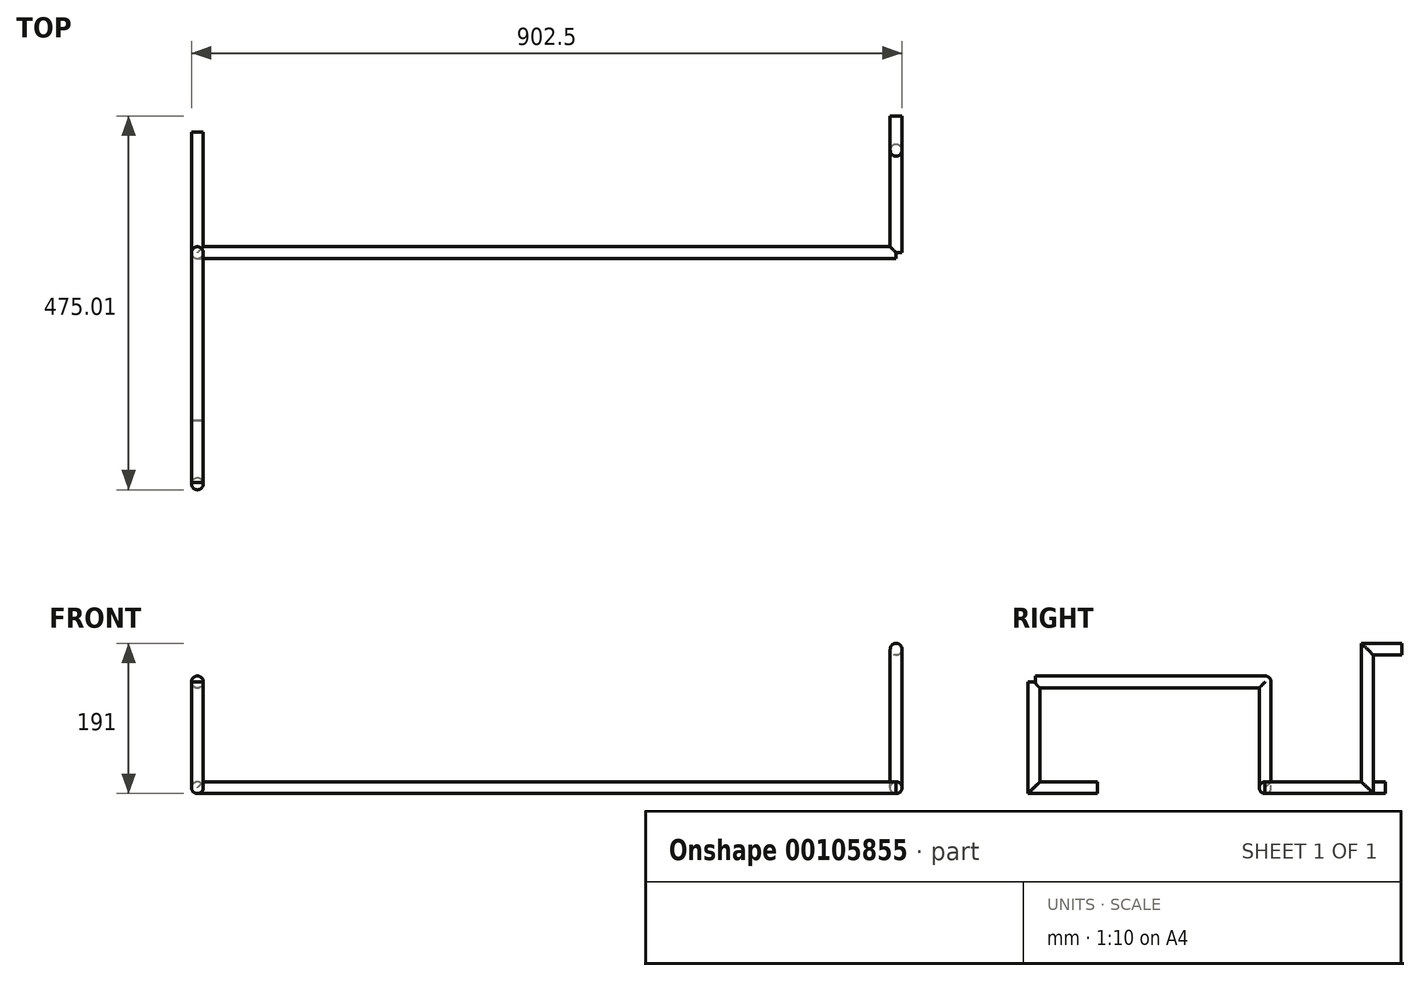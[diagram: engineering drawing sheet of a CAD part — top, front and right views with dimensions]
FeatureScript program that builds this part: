
annotation { "Feature Type Name" : "Feature", "Feature Type Description" : "" }
export const myFeature = defineFeature(function(context is Context, id is Id, definition is map)
    precondition{}
    {
        {
            var Q0;
            Q0=qCreatedBy(makeId("Front.planeOp"),FACE);
            var sketch = newSketch(context, id + "F0", { "sketchPlane" : qUnion([Q0])});
            skCircle(sketch, "E0", {"center": v(0, 0) * mm, "radius": 7.5 * mm});
            skSolve(sketch);
        }
        {
            var Q0;
            Q0=qCreatedBy(makeId("Right.planeOp"),FACE);
            var sketch = newSketch(context, id + "F1", { "sketchPlane" : qUnion([Q0])});
            skLineSegment(sketch, "E1", {"start": v(-80.78, 0) * mm, "end": v(0, 0) * mm});
            skLineSegment(sketch, "E2", {"start": v(-80.78, 0) * mm, "end": v(-80.78, 134.38) * mm});
            skSolve(sketch);
        }
        {
            var Q0;
            Q0=makeQuery(id+"F0.imprint","IMPRINT",FACE,{"disambiguationData":[TD([[makeQuery(id+"F0.imprint","IMPRINT",EDGE,{"derivedFrom":sQuery(id+"F0.wireOp",EDGE,"E0")}),1.0]])]});
            var Q1;
            Q1=sQuery(id+"F1.wireOp",EDGE,"E1");
            var Q2;
            Q2=sQuery(id+"F1.wireOp",EDGE,"E2");
            sweep(context, id + "F2", {"profiles" : qUnion([Q0]), "path" : qUnion([Q1, Q2])});
        }
        {
            var Q0;
            Q0=qCreatedBy(makeId("Top.planeOp"),FACE);
            var sketch = newSketch(context, id + "F3", { "sketchPlane" : qUnion([Q0])});
            skLineSegment(sketch, "E3", {"start": v(0, 276.33) * mm, "end": v(0, 123.33) * mm});
            skSolve(sketch);
        }
        {
            var Q0;
            Q0=qCreatedBy(makeId("Front.planeOp"),FACE);
            cPlane(context, id + "F4", {"entities" : qUnion([Q0]), "cplaneType" : CPlaneType.OFFSET, "offset" : 366 * mm, "oppositeDirection" : true, "width" : 150 * mm, "height" : 150 * mm});
        }
        {
            var Q0;
            Q0=qCreatedBy(id+"F4.planeOp",FACE);
            var sketch = newSketch(context, id + "F5", { "sketchPlane" : qUnion([Q0])});
            skCircle(sketch, "E4", {"center": v(0, 0) * mm, "radius": 7.5 * mm});
            skSolve(sketch);
        }
        {
            var Q0;
            Q0=makeQuery(id+"F5.imprint","IMPRINT",FACE,{"disambiguationData":[TD([[makeQuery(id+"F5.imprint","IMPRINT",EDGE,{"derivedFrom":sQuery(id+"F5.wireOp",EDGE,"E4")}),1.0]])]});
            var Q1;
            Q1=sQuery(id+"F3.wireOp",EDGE,"E3");
            sweep(context, id + "F6", {"profiles" : qUnion([Q0]), "path" : qUnion([Q1])});
        }
        {
            var Q0;
            Q0=qCreatedBy(makeId("Top.planeOp"),FACE);
            var sketch = newSketch(context, id + "F7", { "sketchPlane" : qUnion([Q0])});
            skCircle(sketch, "E5", {"center": v(0, 213) * mm, "radius": 7.5 * mm});
            skSolve(sketch);
        }
        {
            var Q0;
            Q0=makeQuery(id+"F7.imprint","IMPRINT",FACE,{"disambiguationData":[TD([[makeQuery(id+"F7.imprint","IMPRINT",EDGE,{"derivedFrom":sQuery(id+"F7.wireOp",EDGE,"E5")}),1.0]])]});
            var Q1;
            Q1=sQuery(id+"F1.wireOp",EDGE,"E2");
            sweep(context, id + "F8", {"operationType" : NewBodyOperationType.ADD, "profiles" : qUnion([Q0]), "path" : qUnion([Q1])});
        }
        {
            var Q0;
            Q0=qCreatedBy(makeId("Front.planeOp"),FACE);
            cPlane(context, id + "F9", {"entities" : qUnion([Q0]), "cplaneType" : CPlaneType.OFFSET, "offset" : 213 * mm, "oppositeDirection" : true, "width" : 150 * mm, "height" : 150 * mm});
        }
        {
            var Q0;
            Q0=qCreatedBy(id+"F9.planeOp",FACE);
            var sketch = newSketch(context, id + "F10", { "sketchPlane" : qUnion([Q0])});
            skCircle(sketch, "E6", {"center": v(0, 134.38) * mm, "radius": 7.5 * mm});
            skSolve(sketch);
        }
        {
            var Q0;
            Q0=qCreatedBy(makeId("Right.planeOp"),FACE);
            var sketch = newSketch(context, id + "F11", { "sketchPlane" : qUnion([Q0])});
            skLineSegment(sketch, "E7", {"start": v(211.22, 134.38) * mm, "end": v(-80.78, 134.38) * mm});
            skSolve(sketch);
        }
        {
            var Q0;
            Q0=makeQuery(id+"F10.imprint","IMPRINT",FACE,{"disambiguationData":[TD([[makeQuery(id+"F10.imprint","IMPRINT",EDGE,{"derivedFrom":sQuery(id+"F10.wireOp",EDGE,"E6")}),1.0]])]});
            var Q1;
            Q1=sQuery(id+"F11.wireOp",EDGE,"E7");
            sweep(context, id + "F12", {"operationType" : NewBodyOperationType.ADD, "profiles" : qUnion([Q0]), "path" : qUnion([Q1])});
        }
        {
            var Q0;
            Q0=makeQuery(id+"F8.opSweep","CAP_FACE",FACE,{"disambiguationData":[OSD([sQuery(id+"F1.wireOp",VERTEX,"E2.end"),sQuery(id+"F7.wireOp",EDGE,"E5")])],"isStart":false});
            var Q1;
            Q1=makeQuery(id+"F12.boolean.opBoolean","INTERSECT",EDGE,{"derivedFrom":[makeQuery(id+"F8.opSweep","CAP_FACE",FACE,{"disambiguationData":[OSD([sQuery(id+"F1.wireOp",VERTEX,"E2.end"),sQuery(id+"F7.wireOp",EDGE,"E5")])],"isStart":false}),makeQuery(id+"F12.opSweep","CAP_FACE",FACE,{"disambiguationData":[OSD([sQuery(id+"F10.wireOp",EDGE,"E6"),sQuery(id+"F11.wireOp",VERTEX,"E7.start")])],"isStart":true})]});
            revolve(context, id + "F13", {"operationType" : NewBodyOperationType.ADD, "entities" : qUnion([Q0]), "axis" : qUnion([Q1]), "revolveType" : RevolveType.FULL});
        }
        {
            var Q0;
            Q0=makeQuery(id+"F8.opSweep","CAP_FACE",FACE,{"disambiguationData":[OSD([sQuery(id+"F1.wireOp",VERTEX,"E2.start"),sQuery(id+"F7.wireOp",EDGE,"E5")])],"isStart":true});
            var Q1;
            Q1=makeQuery(id+"F8.boolean.opBoolean","INTERSECT",EDGE,{"derivedFrom":[makeQuery(id+"F6.opSweep","CAP_FACE",FACE,{"disambiguationData":[OSD([sQuery(id+"F3.wireOp",VERTEX,"E3.end"),sQuery(id+"F5.wireOp",EDGE,"E4")])],"isStart":false}),makeQuery(id+"F8.opSweep","CAP_FACE",FACE,{"disambiguationData":[OSD([sQuery(id+"F1.wireOp",VERTEX,"E2.start"),sQuery(id+"F7.wireOp",EDGE,"E5")])],"isStart":true})]});
            revolve(context, id + "F14", {"operationType" : NewBodyOperationType.ADD, "entities" : qUnion([Q0]), "axis" : qUnion([Q1]), "revolveType" : RevolveType.FULL});
        }
        {
            var Q0;
            Q0=qCreatedBy(makeId("Right.planeOp"),FACE);
            var sketch = newSketch(context, id + "F15", { "sketchPlane" : qUnion([Q0])});
            skCircle(sketch, "E8", {"center": v(213, 0) * mm, "radius": 7.5 * mm});
            skSolve(sketch);
        }
        {
            var Q0;
            Q0=qCreatedBy(id+"F9.planeOp",FACE);
            var sketch = newSketch(context, id + "F16", { "sketchPlane" : qUnion([Q0])});
            skLineSegment(sketch, "E9", {"start": v(0, 0) * mm, "end": v(887.5, 0) * mm});
            skSolve(sketch);
        }
        {
            var Q0;
            Q0 = qSketchRegion(id + "F15", true);
            var Q1;
            Q1=sQuery(id+"F16.wireOp",EDGE,"E9");
            sweep(context, id + "F17", {"operationType" : NewBodyOperationType.ADD, "profiles" : qUnion([Q0]), "path" : qUnion([Q1])});
        }
        {
            var Q0;
            Q0=qCreatedBy(makeId("Right.planeOp"),FACE);
            var sketch = newSketch(context, id + "F18", { "sketchPlane" : qUnion([Q0])});
            skLineSegment(sketch, "E10", {"start": v(213, 0) * mm, "end": v(343, 0) * mm});
            skLineSegment(sketch, "E11", {"start": v(343, 0) * mm, "end": v(343, 176) * mm});
            skLineSegment(sketch, "E12", {"start": v(343, 176) * mm, "end": v(386.73, 176) * mm});
            skSolve(sketch);
        }
        {
            var Q0;
            Q0=qCreatedBy(id+"F9.planeOp",FACE);
            var sketch = newSketch(context, id + "F19", { "sketchPlane" : qUnion([Q0])});
            skCircle(sketch, "E13", {"center": v(887.5, 0) * mm, "radius": 7.5 * mm});
            skSolve(sketch);
        }
        {
            var Q0;
            Q0=makeQuery(id+"F19.imprint","IMPRINT",FACE,{"disambiguationData":[TD([[makeQuery(id+"F19.imprint","IMPRINT",EDGE,{"derivedFrom":sQuery(id+"F19.wireOp",EDGE,"E13")}),1.0]])]});
            var Q1;
            Q1=sQuery(id+"F18.wireOp",EDGE,"E11");
            var Q2;
            Q2=sQuery(id+"F18.wireOp",EDGE,"E12");
            var Q3;
            Q3=sQuery(id+"F18.wireOp",EDGE,"E10");
            sweep(context, id + "F20", {"operationType" : NewBodyOperationType.ADD, "profiles" : qUnion([Q0]), "path" : qUnion([Q1, Q2, Q3])});
        }
    });
